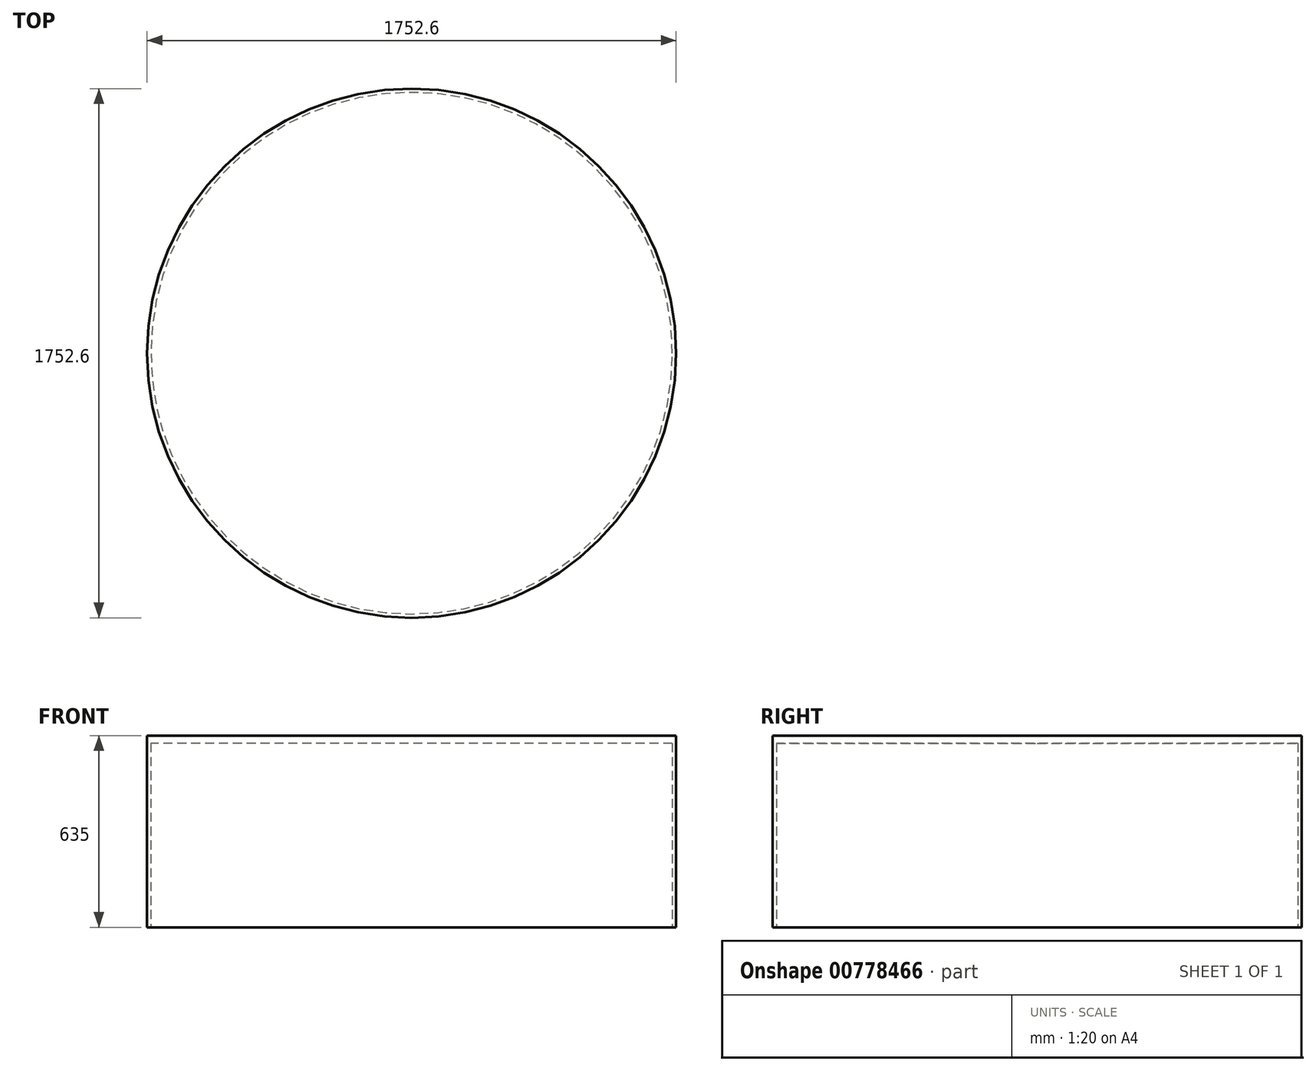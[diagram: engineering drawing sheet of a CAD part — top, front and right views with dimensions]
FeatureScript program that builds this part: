
annotation { "Feature Type Name" : "Feature", "Feature Type Description" : "" }
export const myFeature = defineFeature(function(context is Context, id is Id, definition is map)
    precondition{}
    {
        {
            var Q0;
            Q0=qCreatedBy(makeId("Top.planeOp"),FACE);
            var sketch = newSketch(context, id + "F0", { "sketchPlane" : qUnion([Q0])});
            skCircle(sketch, "E0", {"center": v(0, 0) * mm, "radius": 876.3 * mm});
            skSolve(sketch);
        }
        {
            var Q0;
            Q0 = qSketchRegion(id + "F0", true);
            extrude(context, id + "F1", {"entities" : qUnion([Q0]), "depth" : 635 * mm, "offsetDistance" : 25.4 * mm});
        }
        {
            var Q0;
            Q0 = qSketchRegion(id + "F0", true);
            var sketch = newSketch(context, id + "F2", { "sketchPlane" : qUnion([Q0])});
            skCircle(sketch, "E1", {"center": v(0, 0) * mm, "radius": 863.6 * mm});
            skSolve(sketch);
        }
        {
            var Q0;
            Q0 = qSketchRegion(id + "F2", true);
            extrude(context, id + "F3", {"entities" : qUnion([Q0]), "operationType" : NewBodyOperationType.REMOVE, "depth" : 609.6 * mm, "offsetDistance" : 25.4 * mm});
        }
    });
